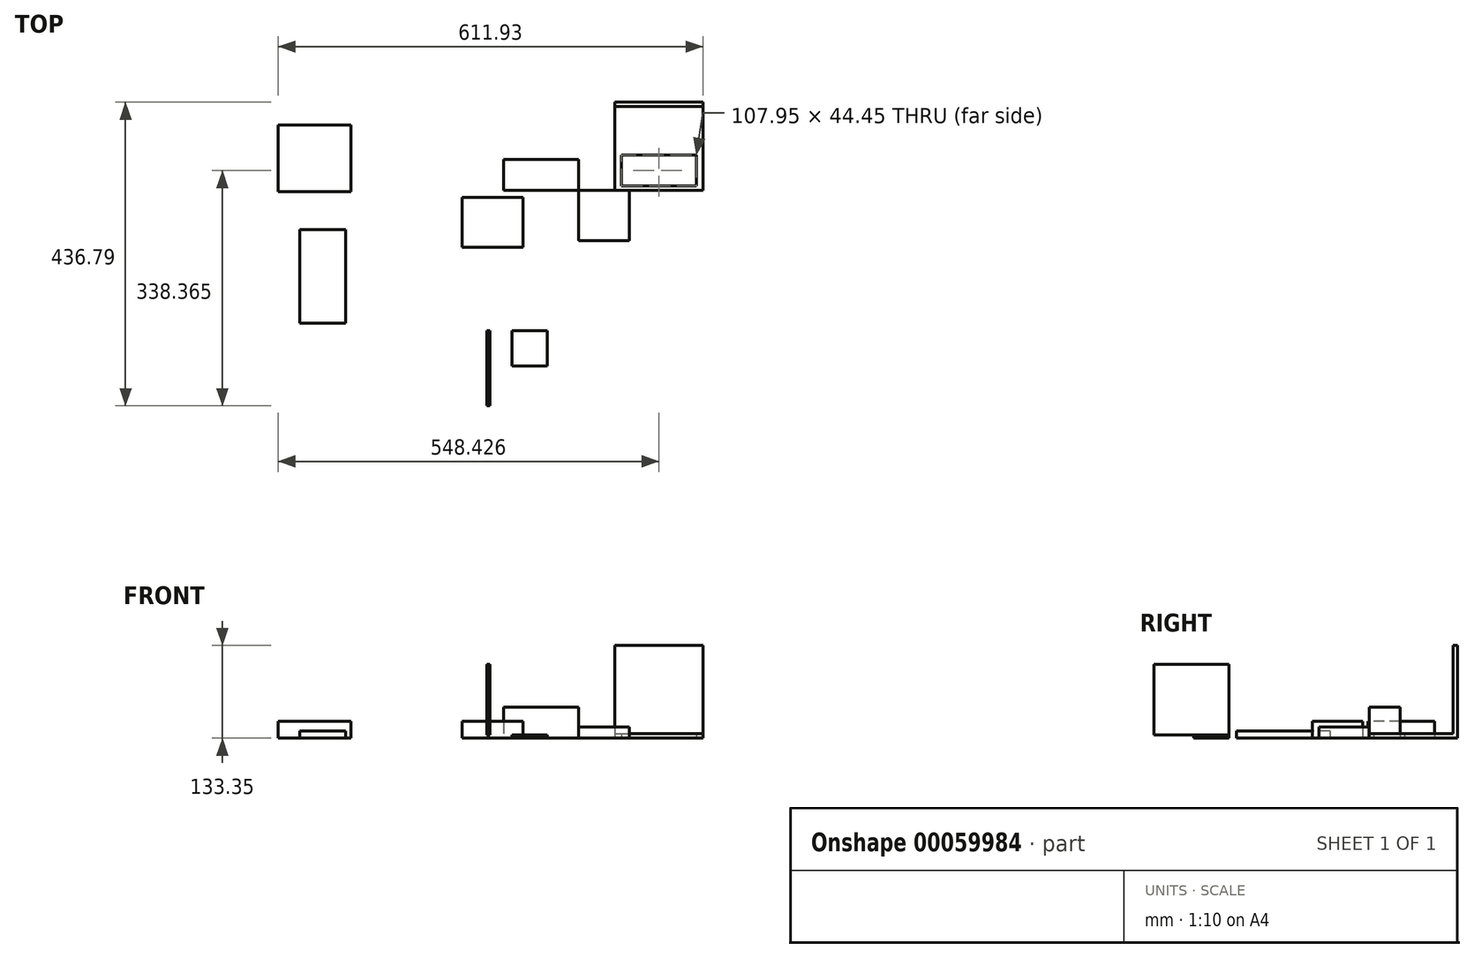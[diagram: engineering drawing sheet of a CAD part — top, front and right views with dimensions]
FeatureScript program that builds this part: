
annotation { "Feature Type Name" : "Feature", "Feature Type Description" : "" }
export const myFeature = defineFeature(function(context is Context, id is Id, definition is map)
    precondition{}
    {
        {
            var Q0;
            Q0=qCreatedBy(makeId("Top.planeOp"),FACE);
            var sketch = newSketch(context, id + "F0", { "sketchPlane" : qUnion([Q0])});
            skLineSegment(sketch, "E0.bottom", {"start": v(-107.95, 44.45) * mm, "end": v(0, 44.45) * mm});
            skLineSegment(sketch, "E0.top", {"start": v(-107.95, 0) * mm, "end": v(0, 0) * mm});
            skLineSegment(sketch, "E0.left", {"start": v(-107.95, 44.45) * mm, "end": v(-107.95, 0) * mm});
            skLineSegment(sketch, "E0.right", {"start": v(0, 44.45) * mm, "end": v(0, 0) * mm});
            skSolve(sketch);
        }
        {
            var Q0;
            Q0=makeQuery(id+"F0.imprint","IMPRINT",FACE,{"disambiguationData":[TD([[makeQuery(id+"F0.imprint","IMPRINT",EDGE,{"derivedFrom":sQuery(id+"F0.wireOp",EDGE,"E0.bottom")}),-1.0]])]});
            extrude(context, id + "F1", {"entities" : qUnion([Q0]), "depth" : 44.45 * mm});
        }
        {
            var Q0;
            Q0=qCreatedBy(makeId("Top.planeOp"),FACE);
            var sketch = newSketch(context, id + "F2", { "sketchPlane" : qUnion([Q0])});
            skLineSegment(sketch, "E1.bottom", {"start": v(0, 0) * mm, "end": v(73.15, 0) * mm});
            skLineSegment(sketch, "E1.top", {"start": v(0, -72.14) * mm, "end": v(73.15, -72.14) * mm});
            skLineSegment(sketch, "E1.left", {"start": v(0, 0) * mm, "end": v(0, -72.14) * mm});
            skLineSegment(sketch, "E1.right", {"start": v(73.15, 0) * mm, "end": v(73.15, -72.14) * mm});
            skSolve(sketch);
        }
        {
            var Q0;
            Q0=makeQuery(id+"F2.imprint","IMPRINT",FACE,{"disambiguationData":[TD([[makeQuery(id+"F2.imprint","IMPRINT",EDGE,{"derivedFrom":sQuery(id+"F2.wireOp",EDGE,"E1.bottom")}),-1.0]])]});
            extrude(context, id + "F3", {"entities" : qUnion([Q0]), "depth" : 16.26 * mm});
        }
        {
            var Q0;
            Q0=qCreatedBy(makeId("Top.planeOp"),FACE);
            var sketch = newSketch(context, id + "F4", { "sketchPlane" : qUnion([Q0])});
            skLineSegment(sketch, "E2.bottom", {"start": v(-167.83, -9.68) * mm, "end": v(-79.69, -9.68) * mm});
            skLineSegment(sketch, "E2.top", {"start": v(-167.83, -81.82) * mm, "end": v(-79.69, -81.82) * mm});
            skLineSegment(sketch, "E2.left", {"start": v(-167.83, -9.68) * mm, "end": v(-167.83, -81.82) * mm});
            skLineSegment(sketch, "E2.right", {"start": v(-79.69, -9.68) * mm, "end": v(-79.69, -81.82) * mm});
            skSolve(sketch);
        }
        {
            var Q0;
            Q0 = qSketchRegion(id + "F4", true);
            extrude(context, id + "F5", {"entities" : qUnion([Q0]), "depth" : 24.13 * mm});
        }
        {
            var Q0;
            Q0=qCreatedBy(makeId("Top.planeOp"),FACE);
            var sketch = newSketch(context, id + "F6", { "sketchPlane" : qUnion([Q0])});
            skLineSegment(sketch, "E3.bottom", {"start": v(-432.66, 94.04) * mm, "end": v(-327.5, 94.04) * mm});
            skLineSegment(sketch, "E3.top", {"start": v(-432.66, -1.97) * mm, "end": v(-327.5, -1.97) * mm});
            skLineSegment(sketch, "E3.left", {"start": v(-432.66, 94.04) * mm, "end": v(-432.66, -1.97) * mm});
            skLineSegment(sketch, "E3.right", {"start": v(-327.5, 94.04) * mm, "end": v(-327.5, -1.97) * mm});
            skSolve(sketch);
        }
        {
            var Q0;
            Q0=makeQuery(id+"F6.imprint","IMPRINT",FACE,{"disambiguationData":[TD([[makeQuery(id+"F6.imprint","IMPRINT",EDGE,{"derivedFrom":sQuery(id+"F6.wireOp",EDGE,"E3.bottom")}),-1.0]])]});
            extrude(context, id + "F7", {"entities" : qUnion([Q0]), "depth" : 24.13 * mm});
        }
        {
            var Q0;
            Q0=qCreatedBy(makeId("Top.planeOp"),FACE);
            var sketch = newSketch(context, id + "F8", { "sketchPlane" : qUnion([Q0])});
            skLineSegment(sketch, "E4.bottom", {"start": v(-401.06, -56.37) * mm, "end": v(-335.02, -56.37) * mm});
            skLineSegment(sketch, "E4.top", {"start": v(-401.06, -191) * mm, "end": v(-335.02, -191) * mm});
            skLineSegment(sketch, "E4.left", {"start": v(-401.06, -56.37) * mm, "end": v(-401.06, -191) * mm});
            skLineSegment(sketch, "E4.right", {"start": v(-335.02, -56.37) * mm, "end": v(-335.02, -191) * mm});
            skSolve(sketch);
        }
        {
            var Q0;
            Q0 = qSketchRegion(id + "F8", true);
            extrude(context, id + "F9", {"entities" : qUnion([Q0]), "depth" : 10.16 * mm});
        }
        {
            var Q0;
            Q0=qCreatedBy(makeId("Top.planeOp"),FACE);
            var sketch = newSketch(context, id + "F10", { "sketchPlane" : qUnion([Q0])});
            skLineSegment(sketch, "E5.bottom", {"start": v(52.27, 0) * mm, "end": v(179.27, 0) * mm});
            skLineSegment(sketch, "E5.top", {"start": v(52.27, 127) * mm, "end": v(179.27, 127) * mm});
            skLineSegment(sketch, "E5.left", {"start": v(52.27, 0) * mm, "end": v(52.27, 127) * mm});
            skLineSegment(sketch, "E5.right", {"start": v(179.27, 0) * mm, "end": v(179.27, 127) * mm});
            skLineSegment(sketch, "E6.bottom", {"start": v(61.8, 6.35) * mm, "end": v(169.74, 6.35) * mm});
            skLineSegment(sketch, "E6.top", {"start": v(61.8, 50.8) * mm, "end": v(169.74, 50.8) * mm});
            skLineSegment(sketch, "E6.left", {"start": v(61.8, 6.35) * mm, "end": v(61.8, 50.8) * mm});
            skLineSegment(sketch, "E6.right", {"start": v(169.74, 6.35) * mm, "end": v(169.74, 50.8) * mm});
            skLineSegment(sketch, "E7", {"start": v(61.8, 6.35) * mm, "end": v(52.27, 6.35) * mm, "construction": true});
            skLineSegment(sketch, "E8", {"start": v(169.74, 6.35) * mm, "end": v(179.27, 6.35) * mm, "construction": true});
            skSolve(sketch);
        }
        {
            var Q0;
            Q0=makeQuery(id+"F10.imprint","IMPRINT",FACE,{"disambiguationData":[TD([[makeQuery(id+"F10.imprint","IMPRINT",EDGE,{"derivedFrom":sQuery(id+"F10.wireOp",EDGE,"E5.bottom")}),1.0]])]});
            extrude(context, id + "F11", {"entities" : qUnion([Q0]), "depth" : 6.35 * mm});
        }
        {
            var Q0;
            Q0=makeQuery(id+"F11.opExtrude","CAP_FACE",FACE,{"disambiguationData":[OSD([sQuery(id+"F10.wireOp",EDGE,"E5.bottom"),sQuery(id+"F10.wireOp",EDGE,"E5.top"),sQuery(id+"F10.wireOp",EDGE,"E5.left"),sQuery(id+"F10.wireOp",EDGE,"E5.right"),sQuery(id+"F10.wireOp",EDGE,"E6.bottom"),sQuery(id+"F10.wireOp",EDGE,"E6.top"),sQuery(id+"F10.wireOp",EDGE,"E6.left"),sQuery(id+"F10.wireOp",EDGE,"E6.right")])],"isStart":false});
            var sketch = newSketch(context, id + "F12", { "sketchPlane" : qUnion([Q0])});
            skLineSegment(sketch, "E9.bottom", {"start": v(52.27, 127) * mm, "end": v(179.27, 127) * mm});
            skLineSegment(sketch, "E9.top", {"start": v(52.27, 120.65) * mm, "end": v(179.27, 120.65) * mm});
            skLineSegment(sketch, "E9.left", {"start": v(52.27, 127) * mm, "end": v(52.27, 120.65) * mm});
            skLineSegment(sketch, "E9.right", {"start": v(179.27, 127) * mm, "end": v(179.27, 120.65) * mm});
            skSolve(sketch);
        }
        {
            var Q0;
            Q0 = qSketchRegion(id + "F12", true);
            extrude(context, id + "F13", {"entities" : qUnion([Q0]), "operationType" : NewBodyOperationType.ADD, "depth" : 127 * mm});
        }
        {
            var Q0;
            Q0=qCreatedBy(makeId("Top.planeOp"),FACE);
            var sketch = newSketch(context, id + "F14", { "sketchPlane" : qUnion([Q0])});
            skLineSegment(sketch, "E10.bottom", {"start": v(-132.36, -201.84) * mm, "end": v(-45.05, -201.84) * mm});
            skLineSegment(sketch, "E10.top", {"start": v(-132.36, -366.94) * mm, "end": v(-45.05, -366.94) * mm});
            skLineSegment(sketch, "E10.left", {"start": v(-132.36, -201.84) * mm, "end": v(-132.36, -366.94) * mm});
            skLineSegment(sketch, "E10.right", {"start": v(-45.05, -201.84) * mm, "end": v(-45.05, -366.94) * mm});
            skLineSegment(sketch, "E11.bottom", {"start": v(-51.4, -366.94) * mm, "end": v(-95.85, -366.94) * mm});
            skLineSegment(sketch, "E11.top", {"start": v(-51.4, -258.99) * mm, "end": v(-95.85, -258.99) * mm});
            skLineSegment(sketch, "E11.left", {"start": v(-51.4, -366.94) * mm, "end": v(-51.4, -258.99) * mm});
            skLineSegment(sketch, "E11.right", {"start": v(-95.85, -366.94) * mm, "end": v(-95.85, -258.99) * mm});
            skLineSegment(sketch, "E12.bottom", {"start": v(-127.6, -207.42) * mm, "end": v(-102.2, -207.42) * mm});
            skLineSegment(sketch, "E12.top", {"start": v(-127.6, -303.44) * mm, "end": v(-102.2, -303.44) * mm});
            skLineSegment(sketch, "E12.left", {"start": v(-127.6, -207.42) * mm, "end": v(-127.6, -303.44) * mm});
            skLineSegment(sketch, "E12.right", {"start": v(-102.2, -207.42) * mm, "end": v(-102.2, -303.44) * mm});
            skLineSegment(sketch, "E13.bottom", {"start": v(-45.05, -201.84) * mm, "end": v(-95.85, -201.84) * mm});
            skLineSegment(sketch, "E13.top", {"start": v(-45.05, -252.64) * mm, "end": v(-95.85, -252.64) * mm});
            skLineSegment(sketch, "E13.left", {"start": v(-45.05, -201.84) * mm, "end": v(-45.05, -252.64) * mm});
            skLineSegment(sketch, "E13.right", {"start": v(-95.85, -201.84) * mm, "end": v(-95.85, -252.64) * mm});
            skSolve(sketch);
        }
        {
            var Q0;
            Q0=makeQuery(id+"F14.imprint","IMPRINT",FACE,{"disambiguationData":[TD([[makeQuery(id+"F14.imprint","IMPRINT",EDGE,{"derivedFrom":sQuery(id+"F14.wireOp",EDGE,"E10.bottom")}),-1.0]])]});
            extrude(context, id + "F15", {"entities" : qUnion([Q0]), "depth" : 4.76 * mm});
        }
        {
            var Q0;
            Q0=makeQuery(id+"F15.opExtrude","CAP_FACE",FACE,{"disambiguationData":[OSD([sQuery(id+"F14.wireOp",EDGE,"E10.bottom"),sQuery(id+"F14.wireOp",EDGE,"E10.top"),sQuery(id+"F14.wireOp",EDGE,"E10.left"),sQuery(id+"F14.wireOp",EDGE,"E10.right"),sQuery(id+"F14.wireOp",EDGE,"E11.top"),sQuery(id+"F14.wireOp",EDGE,"E11.left"),sQuery(id+"F14.wireOp",EDGE,"E11.right"),sQuery(id+"F14.wireOp",EDGE,"E12.bottom"),sQuery(id+"F14.wireOp",EDGE,"E12.top"),sQuery(id+"F14.wireOp",EDGE,"E12.left"),sQuery(id+"F14.wireOp",EDGE,"E12.right")])],"isStart":false});
            var sketch = newSketch(context, id + "F16", { "sketchPlane" : qUnion([Q0])});
            skLineSegment(sketch, "E14.bottom", {"start": v(-132.36, -201.84) * mm, "end": v(-127.6, -201.84) * mm});
            skLineSegment(sketch, "E14.top", {"start": v(-132.36, -309.79) * mm, "end": v(-127.6, -309.79) * mm});
            skLineSegment(sketch, "E14.left", {"start": v(-132.36, -201.84) * mm, "end": v(-132.36, -309.79) * mm});
            skLineSegment(sketch, "E14.right", {"start": v(-127.6, -201.84) * mm, "end": v(-127.6, -309.79) * mm});
            skSolve(sketch);
        }
        {
            var Q0;
            Q0=makeQuery(id+"F16.imprint","IMPRINT",FACE,{"disambiguationData":[TD([[makeQuery(id+"F16.imprint","IMPRINT",EDGE,{"derivedFrom":sQuery(id+"F16.wireOp",EDGE,"E14.bottom")}),-1.0]])]});
            extrude(context, id + "F17", {"entities" : qUnion([Q0]), "operationType" : NewBodyOperationType.ADD, "depth" : 101.6 * mm});
        }
    });
